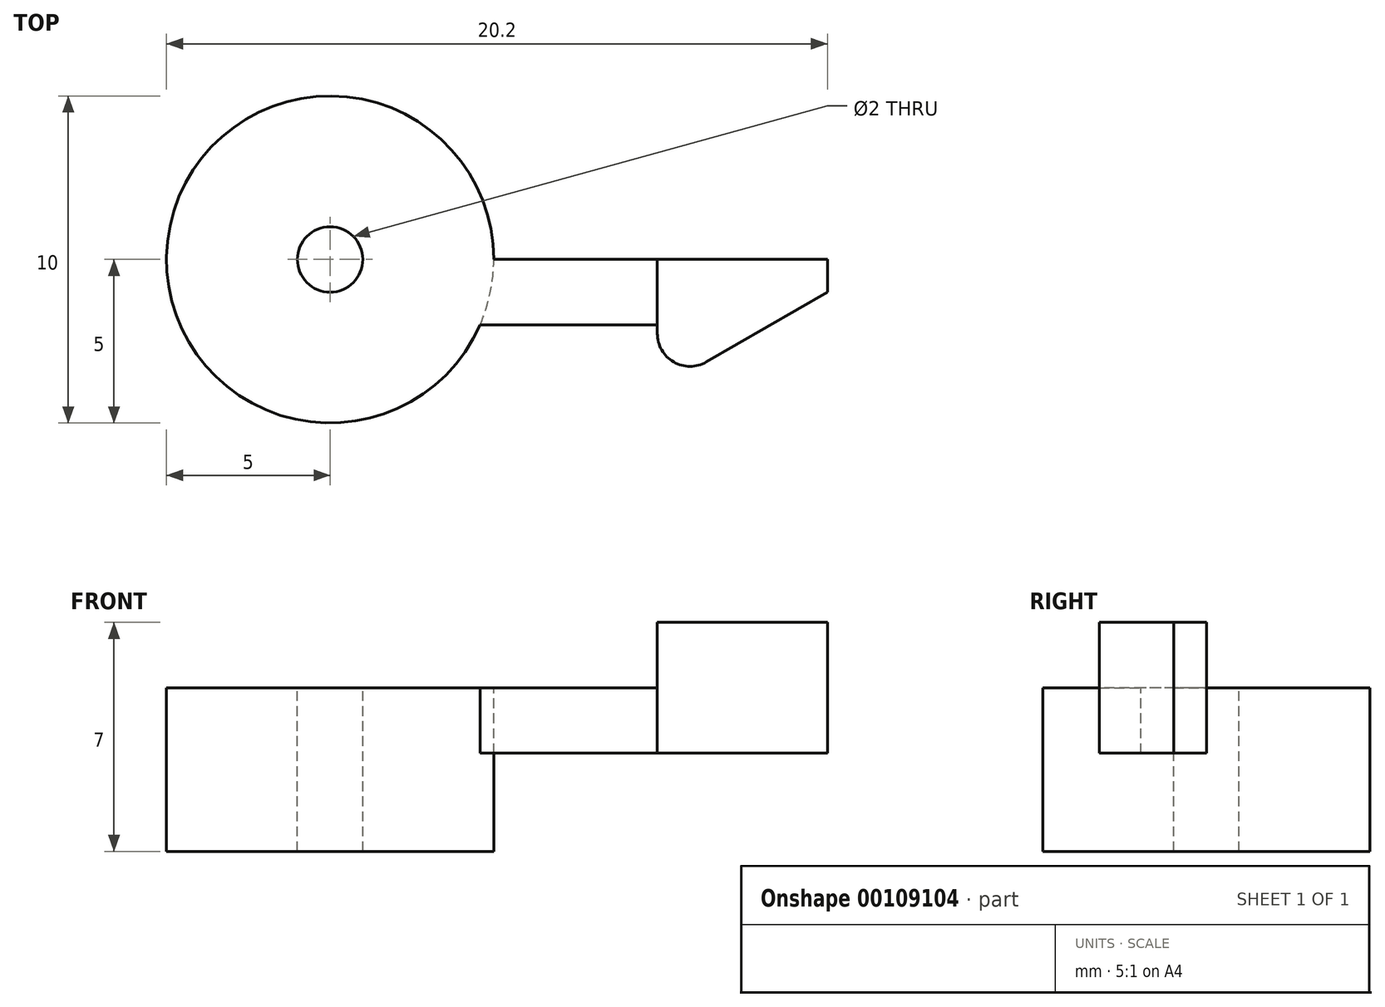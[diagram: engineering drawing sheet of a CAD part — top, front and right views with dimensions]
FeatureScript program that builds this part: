
annotation { "Feature Type Name" : "Feature", "Feature Type Description" : "" }
export const myFeature = defineFeature(function(context is Context, id is Id, definition is map)
    precondition{}
    {
        {
            var Q0;
            Q0=qCreatedBy(makeId("Top.planeOp"),FACE);
            var sketch = newSketch(context, id + "F0", { "sketchPlane" : qUnion([Q0])});
            skCircle(sketch, "E0", {"center": v(0, 0) * mm, "radius": 5 * mm});
            skLineSegment(sketch, "E1", {"start": v(15.2, 0) * mm, "end": v(5, 0) * mm});
            skLineSegment(sketch, "E2.MirrorCS", {"start": v(10, -2) * mm, "end": v(4.58, -2) * mm});
            skLineSegment(sketch, "E3.MirrorCS", {"start": v(10, 0) * mm, "end": v(10, -2) * mm});
            skLineSegment(sketch, "E4.MirrorCS", {"start": v(10, -2) * mm, "end": v(10, -4) * mm});
            skLineSegment(sketch, "E5.MirrorCS", {"start": v(10, -4) * mm, "end": v(15.2, -1) * mm});
            skLineSegment(sketch, "E6.MirrorCS", {"start": v(15.2, -1) * mm, "end": v(15.2, 0) * mm});
            skSolve(sketch);
        }
        {
            var Q0;
            {var subQ0=sQuery(id+"F0.wireOp",EDGE,"E0");var subQ1=makeQuery(id+"F0.imprint","INTERSECT",VERTEX,{"derivedFrom":[subQ0,sQuery(id+"F0.wireOp",EDGE,"E1")]});Q0=makeQuery(id+"F0.imprint","IMPRINT",FACE,{"disambiguationData":[TD([[makeQuery(id+"F0.imprint","IMPRINT",EDGE,{"disambiguationData":[TD([[subQ1,-1.0]])],"derivedFrom":subQ0}),1.0]])]});}
            extrude(context, id + "F1", {"entities" : qUnion([Q0]), "oppositeDirection" : true, "depth" : 5 * mm});
        }
        {
            var Q0;
            {var subQ3=sQuery(id+"F0.wireOp",EDGE,"E2.MirrorCS");Q0=makeQuery(id+"F0.imprint","IMPRINT",FACE,{"disambiguationData":[TD([[makeQuery(id+"F0.imprint","IMPRINT",EDGE,{"derivedFrom":subQ3}),-1.0]])]});}
            extrude(context, id + "F2", {"entities" : qUnion([Q0]), "operationType" : NewBodyOperationType.ADD, "oppositeDirection" : true, "depth" : 2 * mm});
        }
        {
            var Q0;
            {var subQ0=sQuery(id+"F0.wireOp",EDGE,"E3.MirrorCS");Q0=makeQuery(id+"F0.imprint","IMPRINT",FACE,{"disambiguationData":[TD([[makeQuery(id+"F0.imprint","IMPRINT",EDGE,{"derivedFrom":subQ0}),1.0]])]});}
            extrude(context, id + "F3", {"entities" : qUnion([Q0]), "operationType" : NewBodyOperationType.ADD, "endBound" : BoundingType.SYMMETRIC, "depth" : 4 * mm});
        }
        {
            var Q0;
            Q0=makeQuery(id+"F3.opExtrude","SWEPT_EDGE",EDGE,{"disambiguationData":[OSD([sQuery(id+"F0.wireOp",EDGE,"E4.MirrorCS"),sQuery(id+"F0.wireOp",EDGE,"E5.MirrorCS")])]});
            fillet(context, id + "F4", {"entities" : qUnion([Q0]), "radius" : 1 * mm, "tangentPropagation" : true, "allowEdgeOverflow" : false});
        }
        {
            var Q0;
            Q0=sQuery(id+"F0.wireOp",VERTEX,"E0.center");
            var Q1;
            Q1=makeQuery(id+"F1.opExtrude","SWEPT_BODY",BODY,{"disambiguationData":[OSD([sQuery(id+"F0.wireOp",EDGE,"E0")])]});
            hole(context, id + "F5", {"style" : HoleStyle.SIMPLE, "endStyle" : HoleEndStyle.THROUGH, "holeDiameter" : 2 * mm, "locations" : qUnion([Q0]), "scope" : qUnion([Q1]), "isTappedThrough" : true});
        }
    });
